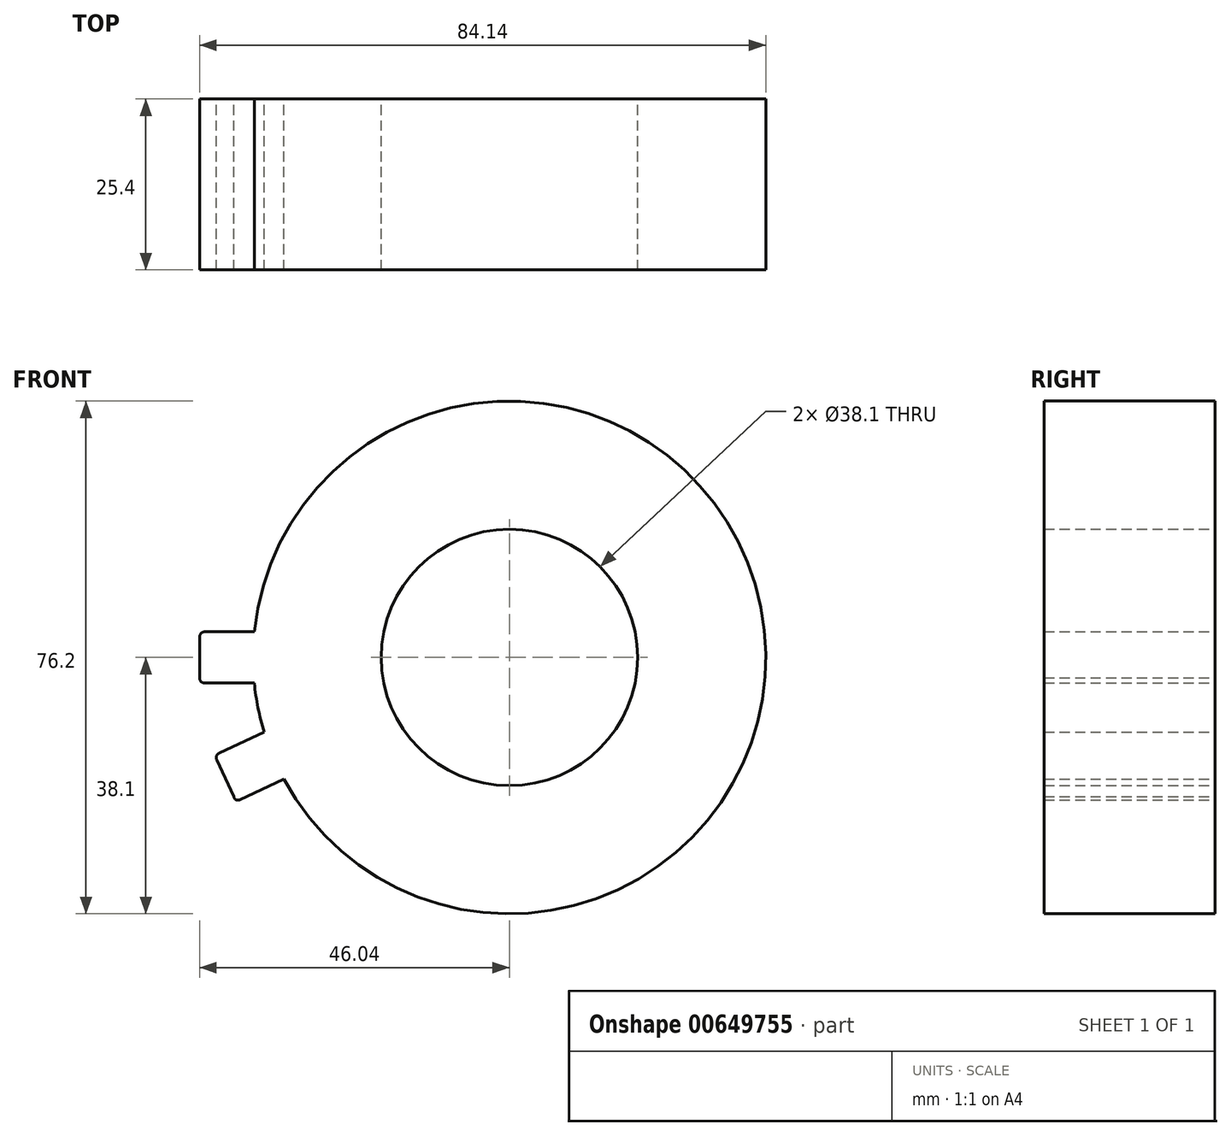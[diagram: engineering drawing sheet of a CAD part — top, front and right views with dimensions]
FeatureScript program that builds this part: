
annotation { "Feature Type Name" : "Feature", "Feature Type Description" : "" }
export const myFeature = defineFeature(function(context is Context, id is Id, definition is map)
    precondition{}
    {
        {
            var Q0;
            Q0=qCreatedBy(makeId("Front.planeOp"),FACE);
            var sketch = newSketch(context, id + "F0", { "sketchPlane" : qUnion([Q0])});
            skCircle(sketch, "E0", {"center": v(0, 0) * mm, "radius": 38.1 * mm});
            skCircle(sketch, "E1", {"center": v(0, 0) * mm, "radius": 19.05 * mm});
            skLineSegment(sketch, "E2", {"start": v(-37.9, 3.8) * mm, "end": v(-45.28, 3.8) * mm});
            skArc(sketch, "E3", {"start": v(-45.28, 3.8) * mm, "mid": v(-45.82, 3.59) * mm, "end": v(-46.04, 3.05) * mm});
            skLineSegment(sketch, "E4", {"start": v(-46.04, 3.05) * mm, "end": v(-46.04, 0) * mm});
            skLineSegment(sketch, "E5", {"start": v(-37.9, -3.81) * mm, "end": v(-45.28, -3.8) * mm});
            skLineSegment(sketch, "E6", {"start": v(-46.04, 0) * mm, "end": v(-46.04, -3.05) * mm});
            skArc(sketch, "E7", {"start": v(-45.28, -3.8) * mm, "mid": v(-45.82, -3.59) * mm, "end": v(-46.04, -3.05) * mm});
            skLineSegment(sketch, "E8", {"start": v(-34.74, 16.06) * mm, "end": v(-41.78, 18.22) * mm});
            skArc(sketch, "E9", {"start": v(-41.78, 18.22) * mm, "mid": v(-42.36, 18.16) * mm, "end": v(-42.74, 17.71) * mm});
            skLineSegment(sketch, "E10", {"start": v(-42.74, 17.71) * mm, "end": v(-43.63, 14.8) * mm});
            skLineSegment(sketch, "E11", {"start": v(-58.61, -59.15) * mm, "end": v(-65.66, -56.99) * mm});
            skLineSegment(sketch, "E12", {"start": v(-43.63, 14.8) * mm, "end": v(-44.52, 11.88) * mm});
            skArc(sketch, "E13", {"start": v(-65.66, -56.99) * mm, "mid": v(-89.52, -11.99) * mm, "end": v(-44.52, 11.88) * mm});
            skLineSegment(sketch, "E14.0", {"start": v(-43.63, 14.8) * mm, "end": v(-42.9, 14.57) * mm, "construction": true});
            skLineSegment(sketch, "E14.1", {"start": v(-42.9, 14.57) * mm, "end": v(-41.78, 18.22) * mm, "construction": true});
            skLineSegment(sketch, "E14.8", {"start": v(-42.74, 17.71) * mm, "end": v(-34.96, 15.33) * mm, "construction": true});
            skLineSegment(sketch, "E14.9", {"start": v(-34.96, 15.33) * mm, "end": v(-34.74, 16.06) * mm, "construction": true});
            skLineSegment(sketch, "E14.16", {"start": v(-41.78, 18.22) * mm, "end": v(-34.74, 16.06) * mm, "construction": true});
            skLineSegment(sketch, "E14.17", {"start": v(-41.78, 18.22) * mm, "end": v(-41.78, 18.22) * mm});
            skLineSegment(sketch, "E14.24", {"start": v(-65.66, -56.99) * mm, "end": v(-58.61, -59.15) * mm, "construction": true});
            skLineSegment(sketch, "E14.25", {"start": v(-65.66, -56.99) * mm, "end": v(-65.66, -56.99) * mm});
            skLineSegment(sketch, "E14.32", {"start": v(-43.63, 14.8) * mm, "end": v(-43.63, 14.8) * mm});
            skLineSegment(sketch, "E14.33", {"start": v(-43.63, 14.8) * mm, "end": v(-42.74, 17.71) * mm, "construction": true});
            skLineSegment(sketch, "E14.40", {"start": v(-42.74, 17.71) * mm, "end": v(-42, 17.49) * mm, "construction": true});
            skLineSegment(sketch, "E14.41", {"start": v(-42, 17.49) * mm, "end": v(-41.78, 18.22) * mm, "construction": true});
            skLineSegment(sketch, "E14.48", {"start": v(-44.52, 11.88) * mm, "end": v(-44.52, 11.88) * mm});
            skLineSegment(sketch, "E14.49", {"start": v(-44.52, 11.88) * mm, "end": v(-43.63, 14.8) * mm, "construction": true});
            skLineSegment(sketch, "E14.56", {"start": v(-65.66, -56.99) * mm, "end": v(-58.61, -59.15) * mm, "construction": true});
            skLineSegment(sketch, "E14.57", {"start": v(-65.66, -56.99) * mm, "end": v(-44.52, 11.88) * mm, "construction": true});
            skLineSegment(sketch, "E15", {"start": v(-36.45, -11.1) * mm, "end": v(-43.13, -14.2) * mm});
            skArc(sketch, "E16", {"start": v(-43.13, -14.2) * mm, "mid": v(-43.52, -14.63) * mm, "end": v(-43.5, -15.22) * mm});
            skLineSegment(sketch, "E17", {"start": v(-43.5, -15.22) * mm, "end": v(-42.23, -17.93) * mm});
            skLineSegment(sketch, "E18", {"start": v(-33.47, -18.05) * mm, "end": v(-40.14, -21.16) * mm});
            skLineSegment(sketch, "E19", {"start": v(-42.23, -17.93) * mm, "end": v(-40.94, -20.7) * mm});
            skArc(sketch, "E20", {"start": v(-40.14, -21.16) * mm, "mid": v(-40.66, -21.14) * mm, "end": v(-40.94, -20.7) * mm});
            skLineSegment(sketch, "E21.0", {"start": v(-42.23, -17.93) * mm, "end": v(-41.54, -17.61) * mm, "construction": true});
            skLineSegment(sketch, "E21.1", {"start": v(-41.54, -17.61) * mm, "end": v(-43.13, -14.2) * mm, "construction": true});
            skLineSegment(sketch, "E21.8", {"start": v(-43.5, -15.22) * mm, "end": v(-36.13, -11.78) * mm, "construction": true});
            skLineSegment(sketch, "E21.9", {"start": v(-36.13, -11.78) * mm, "end": v(-36.45, -11.1) * mm, "construction": true});
            skLineSegment(sketch, "E21.16", {"start": v(-43.13, -14.2) * mm, "end": v(-36.45, -11.1) * mm, "construction": true});
            skLineSegment(sketch, "E21.17", {"start": v(-43.13, -14.2) * mm, "end": v(-43.13, -14.2) * mm});
            skLineSegment(sketch, "E21.24", {"start": v(-40.14, -21.16) * mm, "end": v(-33.47, -18.05) * mm, "construction": true});
            skLineSegment(sketch, "E21.25", {"start": v(-40.14, -21.16) * mm, "end": v(-40.14, -21.16) * mm});
            skLineSegment(sketch, "E21.32", {"start": v(-42.23, -17.93) * mm, "end": v(-42.23, -17.93) * mm});
            skLineSegment(sketch, "E21.33", {"start": v(-42.23, -17.93) * mm, "end": v(-43.5, -15.22) * mm, "construction": true});
            skLineSegment(sketch, "E21.40", {"start": v(-43.5, -15.22) * mm, "end": v(-42.8, -14.9) * mm, "construction": true});
            skLineSegment(sketch, "E21.41", {"start": v(-42.8, -14.9) * mm, "end": v(-43.13, -14.2) * mm, "construction": true});
            skLineSegment(sketch, "E21.48", {"start": v(-40.94, -20.7) * mm, "end": v(-40.94, -20.7) * mm});
            skLineSegment(sketch, "E21.49", {"start": v(-40.94, -20.7) * mm, "end": v(-42.23, -17.93) * mm, "construction": true});
            skLineSegment(sketch, "E21.56", {"start": v(-40.62, -21.39) * mm, "end": v(-33.47, -18.05) * mm, "construction": true});
            skLineSegment(sketch, "E21.57", {"start": v(-40.62, -21.39) * mm, "end": v(-40.94, -20.7) * mm, "construction": true});
            skSolve(sketch);
        }
        {
            var Q0;
            Q0 = qSketchRegion(id + "F0", true);
            extrude(context, id + "F1", {"entities" : qUnion([Q0]), "depth" : 25.4 * mm, "offsetDistance" : 25.4 * mm});
        }
    });
